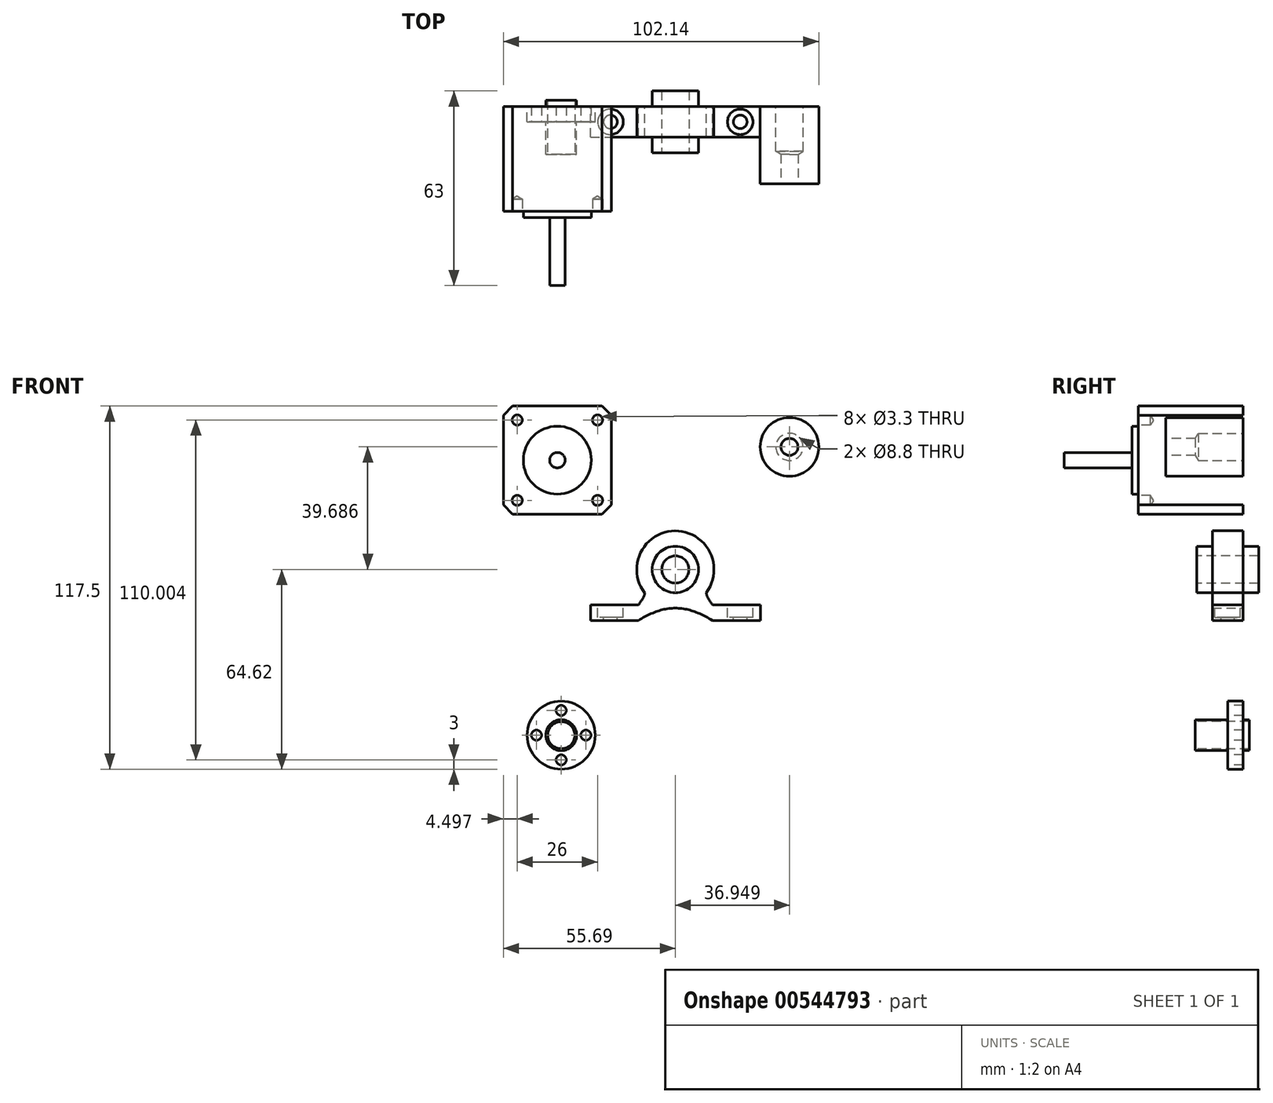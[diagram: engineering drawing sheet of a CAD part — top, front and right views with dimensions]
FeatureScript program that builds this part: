
annotation { "Feature Type Name" : "Feature", "Feature Type Description" : "" }
export const myFeature = defineFeature(function(context is Context, id is Id, definition is map)
    precondition{}
    {
        {
            var Q0;
            Q0=qCreatedBy(makeId("Front.planeOp"),FACE);
            var sketch = newSketch(context, id + "F0", { "sketchPlane" : qUnion([Q0])});
            skLineSegment(sketch, "E0.bottom", {"start": v(-27.5, -11.5) * mm, "end": v(-12, -11.5) * mm});
            skLineSegment(sketch, "E0.top", {"start": v(-27.5, -16.5) * mm, "end": v(-12, -16.5) * mm});
            skLineSegment(sketch, "E0.left", {"start": v(-27.5, -11.5) * mm, "end": v(-27.5, -16.5) * mm});
            skLineSegment(sketch, "E0.right", {"start": v(-12, -11.5) * mm, "end": v(-12, -16.5) * mm});
            skCircle(sketch, "E1", {"center": v(0, 0) * mm, "radius": 12.5 * mm});
            skLineSegment(sketch, "E2.MirrorCS", {"start": v(27.5, -16.5) * mm, "end": v(12, -16.5) * mm});
            skLineSegment(sketch, "E3.MirrorCS", {"start": v(12, -11.5) * mm, "end": v(12, -16.5) * mm});
            skLineSegment(sketch, "E4.MirrorCS", {"start": v(27.5, -11.5) * mm, "end": v(27.5, -16.5) * mm});
            skLineSegment(sketch, "E5.MirrorCS", {"start": v(27.5, -11.5) * mm, "end": v(12, -11.5) * mm});
            skFitSpline(sketch, "E6", {"points": [v(-12, -16.5) * mm, v(0, -12.5) * mm, v(12, -16.5) * mm], "startDerivative": vector(24, 15) * mm, "endDerivative": vector(24, -15) * mm});
            skFitSpline(sketch, "E7", {"points": [v(-12, -11.5) * mm, v(-9.9, -7.64) * mm, v(-12.5, 0) * mm], "startDerivative": vector(6.84, 10.2) * mm, "endDerivative": vector(-7.35, 14.64) * mm});
            skFitSpline(sketch, "E8", {"points": [v(12, -11.5) * mm, v(10.02, -7.48) * mm, v(12.5, 0) * mm], "startDerivative": vector(-6.35, 10.48) * mm, "endDerivative": vector(6.93, 14.4) * mm});
            skCircle(sketch, "E9", {"center": v(0, 0) * mm, "radius": 7.5 * mm});
            skSolve(sketch);
        }
        {
            var Q0;
            Q0=makeQuery(id+"F0.imprint","IMPRINT",FACE,{"disambiguationData":[TD([[makeQuery(id+"F0.imprint","IMPRINT",EDGE,{"derivedFrom":sQuery(id+"F0.wireOp",EDGE,"E1")}),1.0]])]});
            var Q1;
            Q1=makeQuery(id+"F0.imprint","IMPRINT",FACE,{"disambiguationData":[TD([[makeQuery(id+"F0.imprint","IMPRINT",EDGE,{"derivedFrom":sQuery(id+"F0.wireOp",EDGE,"E0.bottom")}),-1.0]])]});
            var Q2;
            Q2=makeQuery(id+"F0.imprint","IMPRINT",FACE,{"disambiguationData":[TD([[makeQuery(id+"F0.imprint","IMPRINT",EDGE,{"derivedFrom":sQuery(id+"F0.wireOp",EDGE,"E2.MirrorCS")}),-1.0]])]});
            var Q3;
            {var subQ0=sQuery(id+"F0.wireOp",EDGE,"E0.right");Q3=makeQuery(id+"F0.imprint","IMPRINT",FACE,{"disambiguationData":[TD([[makeQuery(id+"F0.imprint","IMPRINT",EDGE,{"derivedFrom":subQ0}),1.0]])]});}
            var Q4;
            {var subQ0=sQuery(id+"F0.wireOp",EDGE,"E7");var subQ1=sQuery(id+"F0.wireOp",EDGE,"E1");var subQ2=makeQuery(id+"F0.imprint","INTERSECT",VERTEX,{"disambiguationData":[OD(0.0)],"derivedFrom":[subQ1,subQ0]});Q4=makeQuery(id+"F0.imprint","IMPRINT",FACE,{"disambiguationData":[TD([[makeQuery(id+"F0.imprint","IMPRINT",EDGE,{"disambiguationData":[TD([[subQ2,-1.0]])],"derivedFrom":subQ1}),1.0]])]});}
            var Q5;
            {var subQ5=sQuery(id+"F0.wireOp",EDGE,"E3.MirrorCS");Q5=makeQuery(id+"F0.imprint","IMPRINT",FACE,{"disambiguationData":[TD([[makeQuery(id+"F0.imprint","IMPRINT",EDGE,{"derivedFrom":subQ5}),-1.0]])]});}
            var Q6;
            {var subQ0=sQuery(id+"F0.wireOp",EDGE,"E8");var subQ1=sQuery(id+"F0.wireOp",EDGE,"E1");var subQ2=makeQuery(id+"F0.imprint","INTERSECT",VERTEX,{"disambiguationData":[OD(0.0)],"derivedFrom":[subQ1,subQ0]});Q6=makeQuery(id+"F0.imprint","IMPRINT",FACE,{"disambiguationData":[TD([[makeQuery(id+"F0.imprint","IMPRINT",EDGE,{"disambiguationData":[TD([[subQ2,1.0]])],"derivedFrom":subQ1}),1.0]])]});}
            extrude(context, id + "F1", {"entities" : qUnion([Q0, Q1, Q2, Q3, Q4, Q5, Q6]), "depth" : 10 * mm, "offsetDistance" : 25 * mm});
        }
        {
            var Q0;
            Q0=makeQuery(id+"F1.opExtrude","SWEPT_FACE",FACE,{"disambiguationData":[OSD([sQuery(id+"F0.wireOp",EDGE,"E0.bottom")])]});
            var sketch = newSketch(context, id + "F2", { "sketchPlane" : qUnion([Q0])});
            skPoint(sketch, "E10", {"position": v(-21, -5) * mm});
            skPoint(sketch, "E11.MirrorP", {"position": v(21, -5) * mm});
            skSolve(sketch);
        }
        {
            var Q0;
            Q0=sQuery(id+"F2.wireOp",VERTEX,"E10");
            var Q1;
            Q1=sQuery(id+"F2.wireOp",VERTEX,"E11.MirrorP");
            var Q2;
            Q2=makeQuery(id+"F1.opExtrude","SWEPT_BODY",BODY,{"disambiguationData":[OSD([sQuery(id+"F0.wireOp",EDGE,"E0.bottom"),sQuery(id+"F0.wireOp",EDGE,"E0.top"),sQuery(id+"F0.wireOp",EDGE,"E0.left"),sQuery(id+"F0.wireOp",EDGE,"E1"),sQuery(id+"F0.wireOp",EDGE,"E2.MirrorCS"),sQuery(id+"F0.wireOp",EDGE,"E4.MirrorCS"),sQuery(id+"F0.wireOp",EDGE,"E5.MirrorCS"),sQuery(id+"F0.wireOp",EDGE,"E6"),sQuery(id+"F0.wireOp",EDGE,"E7"),sQuery(id+"F0.wireOp",EDGE,"E8")])]});
            hole(context, id + "F3", {"style" : HoleStyle.C_BORE, "endStyle" : HoleEndStyle.THROUGH, "standardTappedOrClearance" : lookupTablePath({ "standard" : "ISO", "fit" : "Normal", "size" : "M4", "type" : "Clearance" }), "standardBlindInLast" : lookupTablePath({ "fit" : "Standard", "standard" : "ISO", "size" : "M4", "type" : "Clearance" }), "holeDiameter" : 4.4 * mm, "cBoreDiameter" : 8.25 * mm, "cBoreDepth" : 4 * mm, "isTappedThrough" : true, "tappedDepth" : 12 * mm, "tapClearance" : 3, "startFromSketch" : true, "locations" : qUnion([Q0, Q1]), "scope" : qUnion([Q2])});
        }
        {
            var Q0;
            Q0=qCreatedBy(makeId("Front.planeOp"),FACE);
            var sketch = newSketch(context, id + "F4", { "sketchPlane" : qUnion([Q0])});
            skCircle(sketch, "E12", {"center": v(0, 0) * mm, "radius": 7.5 * mm});
            skSolve(sketch);
        }
        {
            var Q0;
            Q0 = qSketchRegion(id + "F4", true);
            extrude(context, id + "F5", {"entities" : qUnion([Q0]), "operationType" : NewBodyOperationType.ADD, "depth" : 15 * mm, "offsetDistance" : 25 * mm, "hasSecondDirection" : true, "secondDirectionOppositeDirection" : true, "secondDirectionDepth" : 5 * mm});
        }
        {
            var Q0;
            Q0=makeQuery(id+"F5.opExtrude","CAP_FACE",FACE,{"disambiguationData":[OSD([sQuery(id+"F4.wireOp",EDGE,"E12")])],"isStart":false});
            var sketch = newSketch(context, id + "F6", { "sketchPlane" : qUnion([Q0])});
            skPoint(sketch, "E13", {"position": v(0, 0) * mm});
            skSolve(sketch);
        }
        {
            var Q0;
            Q0=sQuery(id+"F6.wireOp",VERTEX,"E13");
            var Q1;
            Q1=makeQuery(id+"F1.opExtrude","SWEPT_BODY",BODY,{"disambiguationData":[OSD([sQuery(id+"F0.wireOp",EDGE,"E0.bottom"),sQuery(id+"F0.wireOp",EDGE,"E0.top"),sQuery(id+"F0.wireOp",EDGE,"E0.left"),sQuery(id+"F0.wireOp",EDGE,"E1"),sQuery(id+"F0.wireOp",EDGE,"E2.MirrorCS"),sQuery(id+"F0.wireOp",EDGE,"E4.MirrorCS"),sQuery(id+"F0.wireOp",EDGE,"E5.MirrorCS"),sQuery(id+"F0.wireOp",EDGE,"E6"),sQuery(id+"F0.wireOp",EDGE,"E7"),sQuery(id+"F0.wireOp",EDGE,"E8"),sQuery(id+"F0.wireOp",EDGE,"E9")])]});
            hole(context, id + "F7", {"style" : HoleStyle.SIMPLE, "endStyle" : HoleEndStyle.THROUGH, "standardTappedOrClearance" : lookupTablePath({ "standard" : "ISO", "fit" : "Normal", "size" : "M8", "type" : "Clearance" }), "standardBlindInLast" : lookupTablePath({ "fit" : "Standard", "standard" : "ISO", "size" : "M8", "type" : "Clearance" }), "holeDiameter" : 8.8 * mm, "isTappedThrough" : true, "tappedDepth" : 12 * mm, "tapClearance" : 3, "startFromSketch" : true, "locations" : qUnion([Q0]), "scope" : qUnion([Q1])});
        }
        {
            var Q0;
            Q0=qCreatedBy(makeId("Front.planeOp"),FACE);
            var sketch = newSketch(context, id + "F8", { "sketchPlane" : qUnion([Q0])});
            skLineSegment(sketch, "E14.bottom", {"start": v(-55.7, 52.88) * mm, "end": v(-20.7, 52.88) * mm});
            skLineSegment(sketch, "E14.top", {"start": v(-55.7, 17.88) * mm, "end": v(-20.7, 17.88) * mm});
            skLineSegment(sketch, "E14.left", {"start": v(-55.7, 52.88) * mm, "end": v(-55.7, 17.88) * mm});
            skLineSegment(sketch, "E14.right", {"start": v(-20.7, 52.88) * mm, "end": v(-20.7, 17.88) * mm});
            skSolve(sketch);
        }
        {
            var Q0;
            Q0 = qSketchRegion(id + "F8", true);
            extrude(context, id + "F9", {"entities" : qUnion([Q0]), "depth" : 34 * mm, "offsetDistance" : 25 * mm});
        }
        {
            var Q0;
            Q0=makeQuery(id+"F9.opExtrude","SWEPT_EDGE",EDGE,{"disambiguationData":[OSD([sQuery(id+"F8.wireOp",EDGE,"E14.bottom"),sQuery(id+"F8.wireOp",EDGE,"E14.left")])]});
            var Q1;
            Q1=makeQuery(id+"F9.opExtrude","SWEPT_EDGE",EDGE,{"disambiguationData":[OSD([sQuery(id+"F8.wireOp",EDGE,"E14.bottom"),sQuery(id+"F8.wireOp",EDGE,"E14.right")])]});
            var Q2;
            Q2=makeQuery(id+"F9.opExtrude","SWEPT_EDGE",EDGE,{"disambiguationData":[OSD([sQuery(id+"F8.wireOp",EDGE,"E14.top"),sQuery(id+"F8.wireOp",EDGE,"E14.left")])]});
            var Q3;
            Q3=makeQuery(id+"F9.opExtrude","SWEPT_EDGE",EDGE,{"disambiguationData":[OSD([sQuery(id+"F8.wireOp",EDGE,"E14.top"),sQuery(id+"F8.wireOp",EDGE,"E14.right")])]});
            chamfer(context, id + "F10", {"entities" : qUnion([Q0, Q1, Q2, Q3]), "width" : 3 * mm, "tangentPropagation" : true});
        }
        {
            var Q0;
            Q0=makeQuery(id+"F9.opExtrude","CAP_FACE",FACE,{"disambiguationData":[OSD([sQuery(id+"F8.wireOp",EDGE,"E14.bottom"),sQuery(id+"F8.wireOp",EDGE,"E14.top"),sQuery(id+"F8.wireOp",EDGE,"E14.left"),sQuery(id+"F8.wireOp",EDGE,"E14.right")])],"isStart":false});
            var sketch = newSketch(context, id + "F11", { "sketchPlane" : qUnion([Q0])});
            skPoint(sketch, "E15", {"position": v(-51.2, 48.38) * mm});
            skLineSegment(sketch, "E16", {"start": v(-38.2, 72.5) * mm, "end": v(-38.2, -1.73) * mm, "construction": true});
            skLineSegment(sketch, "E17", {"start": v(-68.57, 35.38) * mm, "end": v(-3.3, 35.38) * mm, "construction": true});
            skPoint(sketch, "E17.endSnap0", {"position": v(-38.2, 35.38) * mm});
            skPoint(sketch, "E18.MirrorP", {"position": v(-25.2, 48.38) * mm});
            skPoint(sketch, "E19.MirrorP", {"position": v(-51.2, 22.38) * mm});
            skPoint(sketch, "E20.MirrorP", {"position": v(-25.2, 22.38) * mm});
            skSolve(sketch);
        }
        {
            var Q0;
            Q0=sQuery(id+"F11.wireOp",VERTEX,"E15");
            var Q1;
            Q1=sQuery(id+"F11.wireOp",VERTEX,"E19.MirrorP");
            var Q2;
            Q2=sQuery(id+"F11.wireOp",VERTEX,"E20.MirrorP");
            var Q3;
            Q3=sQuery(id+"F11.wireOp",VERTEX,"E18.MirrorP");
            var Q4;
            Q4=makeQuery(id+"F9.opExtrude","SWEPT_BODY",BODY,{"disambiguationData":[OSD([sQuery(id+"F8.wireOp",EDGE,"E14.bottom"),sQuery(id+"F8.wireOp",EDGE,"E14.top"),sQuery(id+"F8.wireOp",EDGE,"E14.left"),sQuery(id+"F8.wireOp",EDGE,"E14.right")])]});
            hole(context, id + "F12", {"style" : HoleStyle.SIMPLE, "endStyle" : HoleEndStyle.BLIND, "standardTappedOrClearance" : lookupTablePath({ "standard" : "ISO", "fit" : "Normal", "size" : "M3", "type" : "Clearance" }), "standardBlindInLast" : lookupTablePath({ "fit" : "Standard", "standard" : "ISO", "size" : "M3", "type" : "Clearance" }), "holeDiameter" : 3.3 * mm, "holeDepth" : 4 * mm, "isTappedThrough" : true, "tappedDepth" : 12 * mm, "tapClearance" : 3, "startFromSketch" : true, "locations" : qUnion([Q0, Q1, Q2, Q3]), "scope" : qUnion([Q4])});
        }
        {
            var Q0;
            Q0=makeQuery(id+"F9.opExtrude","CAP_FACE",FACE,{"disambiguationData":[OSD([sQuery(id+"F8.wireOp",EDGE,"E14.bottom"),sQuery(id+"F8.wireOp",EDGE,"E14.top"),sQuery(id+"F8.wireOp",EDGE,"E14.left"),sQuery(id+"F8.wireOp",EDGE,"E14.right")])],"isStart":false});
            var sketch = newSketch(context, id + "F13", { "sketchPlane" : qUnion([Q0])});
            skCircle(sketch, "E21", {"center": v(-38.2, 35.38) * mm, "radius": 11 * mm});
            skSolve(sketch);
        }
        {
            var Q0;
            Q0=makeQuery(id+"F13.imprint","IMPRINT",FACE,{"disambiguationData":[TD([[makeQuery(id+"F13.imprint","IMPRINT",EDGE,{"derivedFrom":sQuery(id+"F13.wireOp",EDGE,"E21")}),1.0]])]});
            extrude(context, id + "F14", {"entities" : qUnion([Q0]), "operationType" : NewBodyOperationType.ADD, "depth" : 2 * mm, "offsetDistance" : 25 * mm});
        }
        {
            var Q0;
            Q0=makeQuery(id+"F14.opExtrude","CAP_FACE",FACE,{"disambiguationData":[OSD([sQuery(id+"F13.wireOp",EDGE,"E21")])],"isStart":false});
            var sketch = newSketch(context, id + "F15", { "sketchPlane" : qUnion([Q0])});
            skCircle(sketch, "E22", {"center": v(-38.2, 35.38) * mm, "radius": 2.5 * mm});
            skSolve(sketch);
        }
        {
            var Q0;
            Q0 = qSketchRegion(id + "F15", true);
            extrude(context, id + "F16", {"entities" : qUnion([Q0]), "operationType" : NewBodyOperationType.ADD, "depth" : 22 * mm, "offsetDistance" : 25 * mm});
        }
        {
            var Q0;
            Q0=qCreatedBy(makeId("Front.planeOp"),FACE);
            var sketch = newSketch(context, id + "F17", { "sketchPlane" : qUnion([Q0])});
            skCircle(sketch, "E23", {"center": v(36.95, 39.69) * mm, "radius": 9.5 * mm});
            skSolve(sketch);
        }
        {
            var Q0;
            Q0 = qSketchRegion(id + "F17", true);
            extrude(context, id + "F18", {"entities" : qUnion([Q0]), "depth" : 25 * mm, "offsetDistance" : 25 * mm});
        }
        {
            var Q0;
            Q0=makeQuery(id+"F18.opExtrude","CAP_FACE",FACE,{"disambiguationData":[OSD([sQuery(id+"F17.wireOp",EDGE,"E23")])],"isStart":false});
            var sketch = newSketch(context, id + "F19", { "sketchPlane" : qUnion([Q0])});
            skPoint(sketch, "E24", {"position": v(36.95, 39.69) * mm});
            skCircle(sketch, "E25", {"center": v(36.95, 39.69) * mm, "radius": 2.5 * mm});
            skSolve(sketch);
        }
        {
            var Q0;
            Q0=sQuery(id+"F19.wireOp",VERTEX,"E24");
            var Q1;
            Q1=makeQuery(id+"F18.opExtrude","SWEPT_BODY",BODY,{"disambiguationData":[OSD([sQuery(id+"F17.wireOp",EDGE,"E23")])]});
            hole(context, id + "F20", {"style" : HoleStyle.SIMPLE, "endStyle" : HoleEndStyle.THROUGH, "standardTappedOrClearance" : lookupTablePath({ "standard" : "ISO", "fit" : "Normal", "size" : "M5", "type" : "Clearance" }), "standardBlindInLast" : lookupTablePath({ "fit" : "Standard", "standard" : "ISO", "size" : "M5", "type" : "Clearance" }), "holeDiameter" : 5.5 * mm, "isTappedThrough" : true, "tappedDepth" : 12 * mm, "tapClearance" : 3, "startFromSketch" : true, "locations" : qUnion([Q0]), "scope" : qUnion([Q1])});
        }
        {
            var Q0;
            Q0=makeQuery(id+"F18.opExtrude","CAP_FACE",FACE,{"disambiguationData":[OSD([sQuery(id+"F17.wireOp",EDGE,"E23")])],"isStart":true});
            var sketch = newSketch(context, id + "F21", { "sketchPlane" : qUnion([Q0])});
            skPoint(sketch, "E26", {"position": v(-36.95, 39.69) * mm});
            skSolve(sketch);
        }
        {
            var Q0;
            Q0=sQuery(id+"F21.wireOp",VERTEX,"E26");
            var Q1;
            Q1=makeQuery(id+"F18.opExtrude","SWEPT_BODY",BODY,{"disambiguationData":[OSD([sQuery(id+"F17.wireOp",EDGE,"E23")])]});
            hole(context, id + "F22", {"style" : HoleStyle.SIMPLE, "endStyle" : HoleEndStyle.BLIND, "standardTappedOrClearance" : lookupTablePath({ "standard" : "ISO", "fit" : "Normal", "size" : "M8", "type" : "Clearance" }), "standardBlindInLast" : lookupTablePath({ "fit" : "Standard", "standard" : "ISO", "size" : "M8", "type" : "Clearance" }), "holeDiameter" : 8.8 * mm, "holeDepth" : 14.5 * mm, "isTappedThrough" : true, "tappedDepth" : 12 * mm, "tapClearance" : 3, "startFromSketch" : true, "locations" : qUnion([Q0]), "scope" : qUnion([Q1])});
        }
        {
            var Q0;
            Q0=qCreatedBy(makeId("Front.planeOp"),FACE);
            var sketch = newSketch(context, id + "F23", { "sketchPlane" : qUnion([Q0])});
            skCircle(sketch, "E27", {"center": v(-36.95, -53.62) * mm, "radius": 11 * mm});
            skSolve(sketch);
        }
        {
            var Q0;
            Q0 = qSketchRegion(id + "F23", true);
            extrude(context, id + "F24", {"entities" : qUnion([Q0]), "depth" : 5 * mm, "offsetDistance" : 25 * mm});
        }
        {
            var Q0;
            Q0=makeQuery(id+"F24.opExtrude","CAP_FACE",FACE,{"disambiguationData":[OSD([sQuery(id+"F23.wireOp",EDGE,"E27")])],"isStart":false});
            var sketch = newSketch(context, id + "F25", { "sketchPlane" : qUnion([Q0])});
            skCircle(sketch, "E28", {"center": v(-36.95, -53.62) * mm, "radius": 5 * mm});
            skSolve(sketch);
        }
        {
            var Q0;
            Q0 = qSketchRegion(id + "F25", true);
            extrude(context, id + "F26", {"entities" : qUnion([Q0]), "operationType" : NewBodyOperationType.ADD, "depth" : 10.5 * mm, "offsetDistance" : 25 * mm, "hasSecondDirection" : true, "secondDirectionOppositeDirection" : true, "secondDirectionDepth" : 7 * mm});
        }
        {
            var Q0;
            Q0=makeQuery(id+"F24.opExtrude","CAP_FACE",FACE,{"disambiguationData":[OSD([sQuery(id+"F23.wireOp",EDGE,"E27")])],"isStart":false});
            var sketch = newSketch(context, id + "F27", { "sketchPlane" : qUnion([Q0])});
            skPoint(sketch, "E29", {"position": v(-36.95, -45.62) * mm});
            skPoint(sketch, "E30", {"position": v(-28.95, -53.62) * mm});
            skPoint(sketch, "E31", {"position": v(-36.95, -61.62) * mm});
            skPoint(sketch, "E32", {"position": v(-44.95, -53.62) * mm});
            skSolve(sketch);
        }
        {
            var Q0;
            Q0=sQuery(id+"F27.wireOp",VERTEX,"E29");
            var Q1;
            Q1=sQuery(id+"F27.wireOp",VERTEX,"E30");
            var Q2;
            Q2=sQuery(id+"F27.wireOp",VERTEX,"E31");
            var Q3;
            Q3=sQuery(id+"F27.wireOp",VERTEX,"E32");
            var Q4;
            Q4=makeQuery(id+"F24.opExtrude","SWEPT_BODY",BODY,{"disambiguationData":[OSD([sQuery(id+"F23.wireOp",EDGE,"E27")])]});
            hole(context, id + "F28", {"style" : HoleStyle.SIMPLE, "endStyle" : HoleEndStyle.THROUGH, "standardTappedOrClearance" : lookupTablePath({ "standard" : "ISO", "fit" : "Normal", "size" : "M3", "type" : "Clearance" }), "standardBlindInLast" : lookupTablePath({ "fit" : "Standard", "standard" : "ISO", "size" : "M3", "type" : "Clearance" }), "holeDiameter" : 3.3 * mm, "isTappedThrough" : true, "tappedDepth" : 12 * mm, "tapClearance" : 3, "startFromSketch" : true, "locations" : qUnion([Q0, Q1, Q2, Q3]), "scope" : qUnion([Q4])});
        }
        {
            var Q0;
            Q0=makeQuery(id+"F26.opExtrude","CAP_FACE",FACE,{"disambiguationData":[OSD([sQuery(id+"F25.wireOp",EDGE,"E28")])],"isStart":false});
            var sketch = newSketch(context, id + "F29", { "sketchPlane" : qUnion([Q0])});
            skPoint(sketch, "E33", {"position": v(-36.95, -53.62) * mm});
            skSolve(sketch);
        }
        {
            var Q0;
            Q0=sQuery(id+"F29.wireOp",VERTEX,"E33");
            var Q1;
            Q1=makeQuery(id+"F24.opExtrude","SWEPT_BODY",BODY,{"disambiguationData":[OSD([sQuery(id+"F23.wireOp",EDGE,"E27")])]});
            hole(context, id + "F30", {"style" : HoleStyle.SIMPLE, "endStyle" : HoleEndStyle.THROUGH, "standardTappedOrClearance" : lookupTablePath({ "standard" : "ISO", "fit" : "Normal", "size" : "M8", "type" : "Clearance" }), "standardBlindInLast" : lookupTablePath({ "fit" : "Standard", "standard" : "ISO", "size" : "M8", "type" : "Clearance" }), "holeDiameter" : 8.8 * mm, "isTappedThrough" : true, "tappedDepth" : 12 * mm, "tapClearance" : 3, "startFromSketch" : true, "locations" : qUnion([Q0]), "scope" : qUnion([Q1])});
        }
    });
